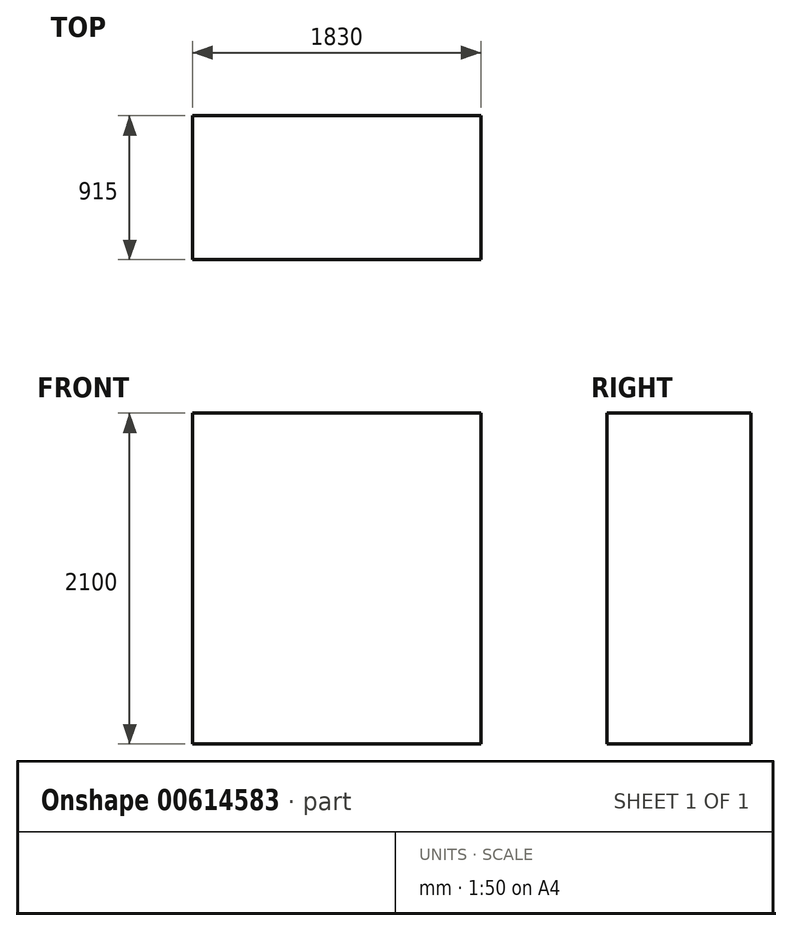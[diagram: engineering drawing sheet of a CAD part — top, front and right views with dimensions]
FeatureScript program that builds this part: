
annotation { "Feature Type Name" : "Feature", "Feature Type Description" : "" }
export const myFeature = defineFeature(function(context is Context, id is Id, definition is map)
    precondition{}
    {
        {
            var Q0;
            Q0=qCreatedBy(makeId("Top.planeOp"),FACE);
            var sketch = newSketch(context, id + "F0", { "sketchPlane" : qUnion([Q0])});
            skLineSegment(sketch, "E0.bottom", {"start": v(0, 0) * mm, "end": v(1830, 0) * mm});
            skLineSegment(sketch, "E0.top", {"start": v(0, -915) * mm, "end": v(1830, -915) * mm});
            skLineSegment(sketch, "E0.left", {"start": v(0, 0) * mm, "end": v(0, -915) * mm});
            skLineSegment(sketch, "E0.right", {"start": v(1830, 0) * mm, "end": v(1830, -915) * mm});
            skSolve(sketch);
        }
        {
            var Q0;
            Q0=makeQuery(id+"F0.imprint","IMPRINT",FACE,{"disambiguationData":[TD([[makeQuery(id+"F0.imprint","IMPRINT",EDGE,{"derivedFrom":sQuery(id+"F0.wireOp",EDGE,"E0.bottom")}),-1.0]])]});
            extrude(context, id + "F1", {"entities" : qUnion([Q0]), "depth" : 2100 * mm, "offsetDistance" : 25 * mm});
        }
    });
